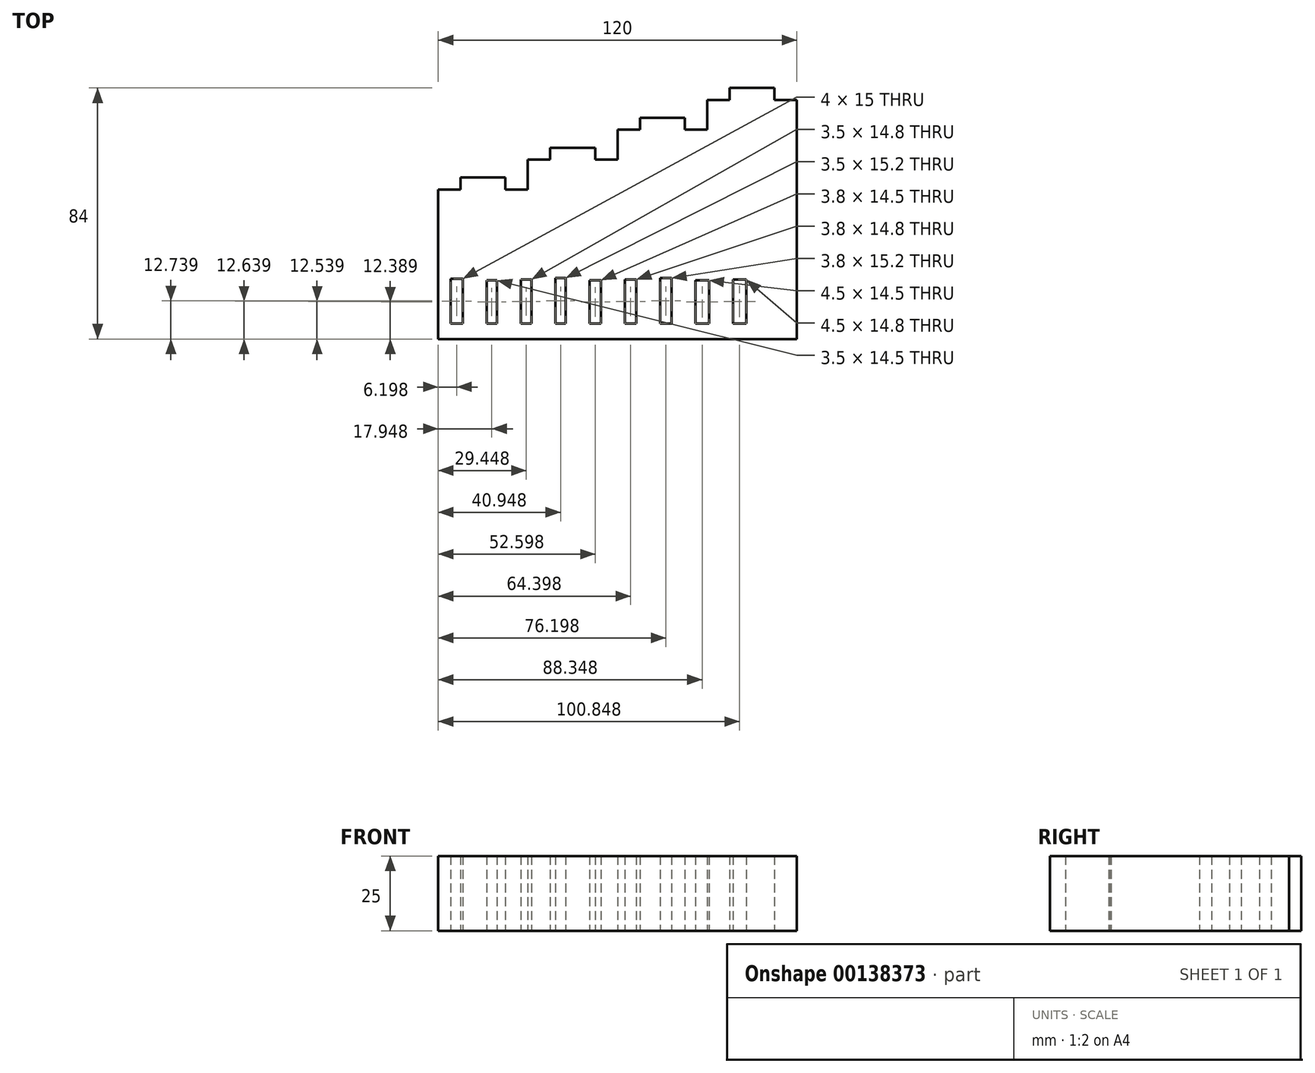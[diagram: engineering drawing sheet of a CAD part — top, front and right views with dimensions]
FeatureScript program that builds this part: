
annotation { "Feature Type Name" : "Feature", "Feature Type Description" : "" }
export const myFeature = defineFeature(function(context is Context, id is Id, definition is map)
    precondition{}
    {
        {
            var Q0;
            Q0=qCreatedBy(makeId("Top.planeOp"),FACE);
            var sketch = newSketch(context, id + "F0", { "sketchPlane" : qUnion([Q0])});
            skLineSegment(sketch, "E0.bottom", {"start": v(30, 40) * mm, "end": v(60, 40) * mm});
            skLineSegment(sketch, "E0.top", {"start": v(-60, -40) * mm, "end": v(60, -40) * mm});
            skLineSegment(sketch, "E0.right", {"start": v(60, 40) * mm, "end": v(60, -40) * mm});
            skPoint(sketch, "E0.middle", {"position": v(0, 0) * mm});
            skLineSegment(sketch, "E1.top", {"start": v(0, 30) * mm, "end": v(30, 30) * mm});
            skLineSegment(sketch, "E1.right", {"start": v(30, 40) * mm, "end": v(30, 30) * mm});
            skLineSegment(sketch, "E2.top", {"start": v(-30, 20) * mm, "end": v(0, 20) * mm});
            skLineSegment(sketch, "E2.right", {"start": v(0, 30) * mm, "end": v(0, 20) * mm});
            skLineSegment(sketch, "E3.top", {"start": v(-60, 10) * mm, "end": v(-30, 10) * mm});
            skLineSegment(sketch, "E3.right", {"start": v(-30, 20) * mm, "end": v(-30, 10) * mm});
            skLineSegment(sketch, "E4.trimOffspring", {"start": v(-60, 10) * mm, "end": v(-60, -40) * mm});
            skPoint(sketch, "E5.orphan", {"position": v(-60, 40) * mm});
            skPoint(sketch, "E6", {"position": v(-45, 10) * mm});
            skPoint(sketch, "E7", {"position": v(-15, 20) * mm});
            skPoint(sketch, "E8", {"position": v(15, 30) * mm});
            skPoint(sketch, "E9", {"position": v(45, 40) * mm});
            skLineSegment(sketch, "E10.bottom", {"start": v(37.5, 40) * mm, "end": v(52.5, 40) * mm});
            skLineSegment(sketch, "E10.top", {"start": v(37.5, 44) * mm, "end": v(52.5, 44) * mm});
            skLineSegment(sketch, "E10.left", {"start": v(37.5, 40) * mm, "end": v(37.5, 44) * mm});
            skLineSegment(sketch, "E10.right", {"start": v(52.5, 40) * mm, "end": v(52.5, 44) * mm});
            skLineSegment(sketch, "E11", {"start": v(45, 40) * mm, "end": v(45, 44) * mm, "construction": true});
            skLineSegment(sketch, "E12.bottom", {"start": v(7.5, 30) * mm, "end": v(22.5, 30) * mm});
            skLineSegment(sketch, "E12.top", {"start": v(7.5, 34) * mm, "end": v(22.5, 34) * mm});
            skLineSegment(sketch, "E12.left", {"start": v(7.5, 30) * mm, "end": v(7.5, 34) * mm});
            skLineSegment(sketch, "E12.right", {"start": v(22.5, 30) * mm, "end": v(22.5, 34) * mm});
            skLineSegment(sketch, "E13.bottom", {"start": v(-7.5, 20) * mm, "end": v(-22.5, 20) * mm});
            skLineSegment(sketch, "E13.top", {"start": v(-7.5, 24) * mm, "end": v(-22.5, 24) * mm});
            skLineSegment(sketch, "E13.left", {"start": v(-7.5, 20) * mm, "end": v(-7.5, 24) * mm});
            skLineSegment(sketch, "E13.right", {"start": v(-22.5, 20) * mm, "end": v(-22.5, 24) * mm});
            skLineSegment(sketch, "E14", {"start": v(15, 30) * mm, "end": v(15, 34) * mm, "construction": true});
            skLineSegment(sketch, "E15", {"start": v(-15, 20) * mm, "end": v(-15, 24) * mm, "construction": true});
            skLineSegment(sketch, "E16.bottom", {"start": v(-52.5, 10) * mm, "end": v(-37.5, 10) * mm});
            skLineSegment(sketch, "E16.top", {"start": v(-52.5, 14) * mm, "end": v(-37.5, 14) * mm});
            skLineSegment(sketch, "E16.left", {"start": v(-52.5, 10) * mm, "end": v(-52.5, 14) * mm});
            skLineSegment(sketch, "E16.right", {"start": v(-37.5, 10) * mm, "end": v(-37.5, 14) * mm});
            skLineSegment(sketch, "E17", {"start": v(-45, 10) * mm, "end": v(-45, 14) * mm, "construction": true});
            skLineSegment(sketch, "E18.bottom", {"start": v(-55.8, -19.86) * mm, "end": v(-51.8, -19.86) * mm});
            skLineSegment(sketch, "E18.top", {"start": v(-55.8, -34.86) * mm, "end": v(-51.8, -34.86) * mm});
            skLineSegment(sketch, "E18.left", {"start": v(-55.8, -19.86) * mm, "end": v(-55.8, -34.86) * mm});
            skLineSegment(sketch, "E18.right", {"start": v(-51.8, -19.86) * mm, "end": v(-51.8, -34.86) * mm});
            skLineSegment(sketch, "E19", {"start": v(-55.8, -34.86) * mm, "end": v(55.84, -34.86) * mm, "construction": true});
            skLineSegment(sketch, "E20.bottom", {"start": v(-43.8, -34.86) * mm, "end": v(-40.3, -34.86) * mm});
            skLineSegment(sketch, "E20.top", {"start": v(-43.8, -20.36) * mm, "end": v(-40.3, -20.36) * mm});
            skLineSegment(sketch, "E20.left", {"start": v(-43.8, -34.86) * mm, "end": v(-43.8, -20.36) * mm});
            skLineSegment(sketch, "E20.right", {"start": v(-40.3, -34.86) * mm, "end": v(-40.3, -20.36) * mm});
            skLineSegment(sketch, "E21.bottom", {"start": v(-32.3, -20.06) * mm, "end": v(-28.8, -20.06) * mm});
            skLineSegment(sketch, "E21.top", {"start": v(-32.3, -34.86) * mm, "end": v(-28.8, -34.86) * mm});
            skLineSegment(sketch, "E21.left", {"start": v(-32.3, -20.06) * mm, "end": v(-32.3, -34.86) * mm});
            skLineSegment(sketch, "E21.right", {"start": v(-28.8, -20.06) * mm, "end": v(-28.8, -34.86) * mm});
            skLineSegment(sketch, "E22.bottom", {"start": v(-20.8, -19.66) * mm, "end": v(-17.3, -19.66) * mm});
            skLineSegment(sketch, "E22.top", {"start": v(-20.8, -34.86) * mm, "end": v(-17.3, -34.86) * mm});
            skLineSegment(sketch, "E22.left", {"start": v(-20.8, -19.66) * mm, "end": v(-20.8, -34.86) * mm});
            skLineSegment(sketch, "E22.right", {"start": v(-17.3, -19.66) * mm, "end": v(-17.3, -34.86) * mm});
            skLineSegment(sketch, "E23.bottom", {"start": v(-9.3, -20.36) * mm, "end": v(-5.5, -20.36) * mm});
            skLineSegment(sketch, "E23.top", {"start": v(-9.3, -34.86) * mm, "end": v(-5.5, -34.86) * mm});
            skLineSegment(sketch, "E23.left", {"start": v(-9.3, -20.36) * mm, "end": v(-9.3, -34.86) * mm});
            skLineSegment(sketch, "E23.right", {"start": v(-5.5, -20.36) * mm, "end": v(-5.5, -34.86) * mm});
            skLineSegment(sketch, "E24.bottom", {"start": v(2.5, -20.06) * mm, "end": v(6.3, -20.06) * mm});
            skLineSegment(sketch, "E24.top", {"start": v(2.5, -34.86) * mm, "end": v(6.3, -34.86) * mm});
            skLineSegment(sketch, "E24.left", {"start": v(2.5, -20.06) * mm, "end": v(2.5, -34.86) * mm});
            skLineSegment(sketch, "E24.right", {"start": v(6.3, -20.06) * mm, "end": v(6.3, -34.86) * mm});
            skLineSegment(sketch, "E25.bottom", {"start": v(14.3, -19.66) * mm, "end": v(18.1, -19.66) * mm});
            skLineSegment(sketch, "E25.top", {"start": v(14.3, -34.86) * mm, "end": v(18.1, -34.86) * mm});
            skLineSegment(sketch, "E25.left", {"start": v(14.3, -19.66) * mm, "end": v(14.3, -34.86) * mm});
            skLineSegment(sketch, "E25.right", {"start": v(18.1, -19.66) * mm, "end": v(18.1, -34.86) * mm});
            skLineSegment(sketch, "E26.bottom", {"start": v(26.1, -20.36) * mm, "end": v(30.6, -20.36) * mm});
            skLineSegment(sketch, "E26.top", {"start": v(26.1, -34.86) * mm, "end": v(30.6, -34.86) * mm});
            skLineSegment(sketch, "E26.left", {"start": v(26.1, -20.36) * mm, "end": v(26.1, -34.86) * mm});
            skLineSegment(sketch, "E26.right", {"start": v(30.6, -20.36) * mm, "end": v(30.6, -34.86) * mm});
            skLineSegment(sketch, "E27.bottom", {"start": v(38.6, -20.06) * mm, "end": v(43.1, -20.06) * mm});
            skLineSegment(sketch, "E27.top", {"start": v(38.6, -34.86) * mm, "end": v(43.1, -34.86) * mm});
            skLineSegment(sketch, "E27.left", {"start": v(38.6, -20.06) * mm, "end": v(38.6, -34.86) * mm});
            skLineSegment(sketch, "E27.right", {"start": v(43.1, -20.06) * mm, "end": v(43.1, -34.86) * mm});
            skSolve(sketch);
        }
        {
            var Q0;
            Q0 = qSketchRegion(id + "F0", true);
            extrude(context, id + "F1", {"entities" : qUnion([Q0]), "depth" : 25 * mm});
        }
    });
